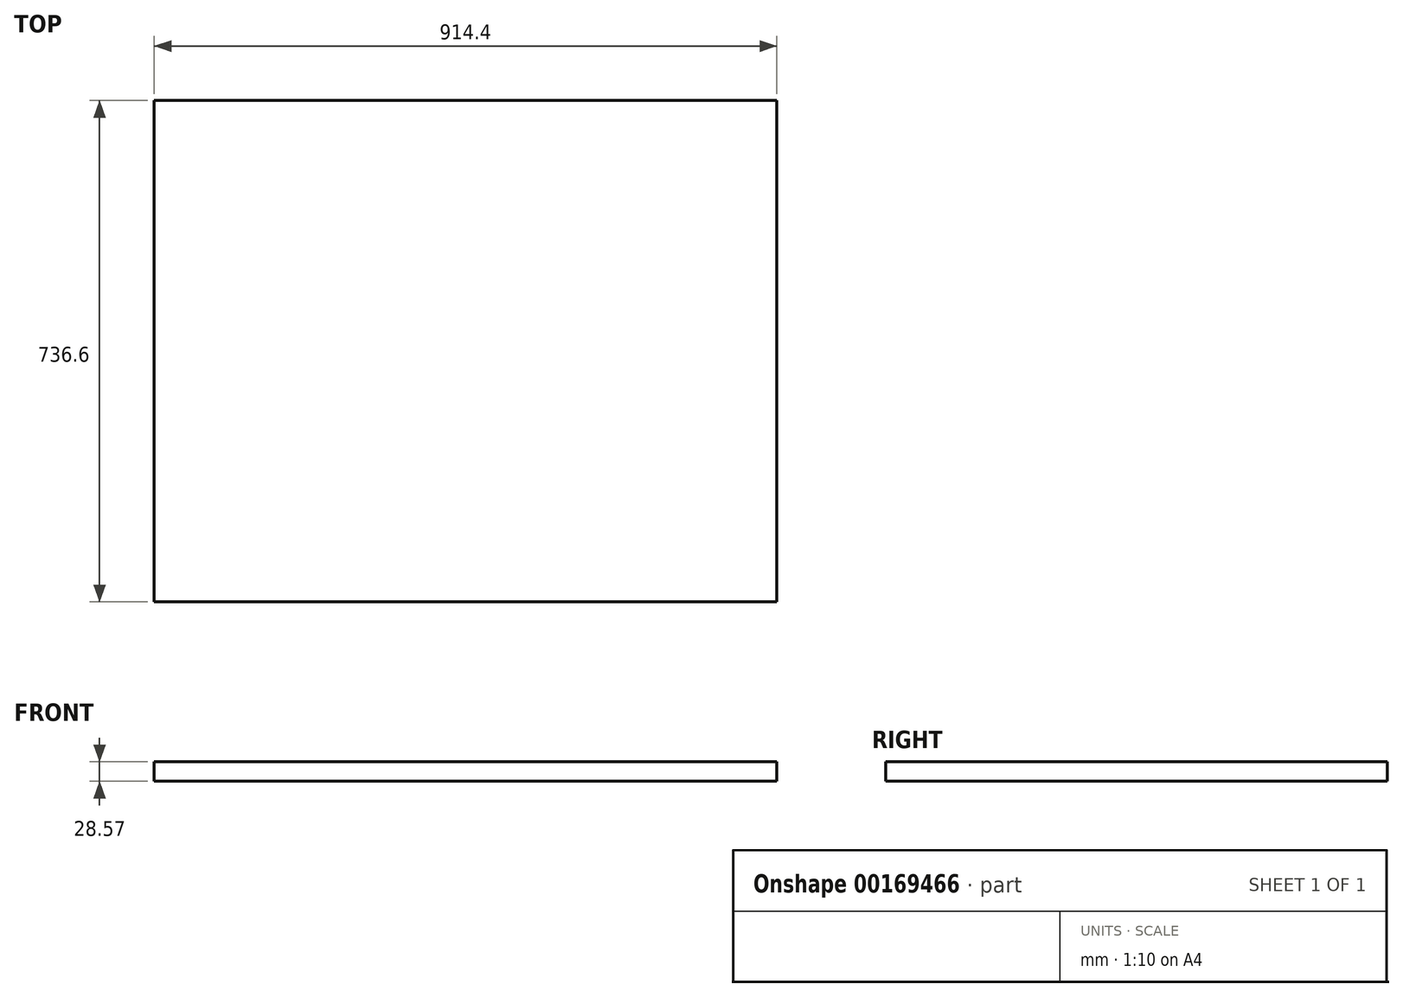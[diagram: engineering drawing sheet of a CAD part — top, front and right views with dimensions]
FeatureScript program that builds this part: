
annotation { "Feature Type Name" : "Feature", "Feature Type Description" : "" }
export const myFeature = defineFeature(function(context is Context, id is Id, definition is map)
    precondition{}
    {
        {
            var Q0;
            Q0=qCreatedBy(makeId("Top.planeOp"),FACE);
            var sketch = newSketch(context, id + "F0", { "sketchPlane" : qUnion([Q0])});
            skLineSegment(sketch, "E0.bottom", {"start": v(-435.66, 422.93) * mm, "end": v(478.74, 422.93) * mm});
            skLineSegment(sketch, "E0.top", {"start": v(-435.66, -313.67) * mm, "end": v(478.74, -313.67) * mm});
            skLineSegment(sketch, "E0.left", {"start": v(-435.66, 422.93) * mm, "end": v(-435.66, -313.67) * mm});
            skLineSegment(sketch, "E0.right", {"start": v(478.74, 422.93) * mm, "end": v(478.74, -313.67) * mm});
            skSolve(sketch);
        }
        {
            var Q0;
            Q0 = qSketchRegion(id + "F0", true);
            extrude(context, id + "F1", {"entities" : qUnion([Q0]), "depth" : 28.57 * mm});
        }
    });
